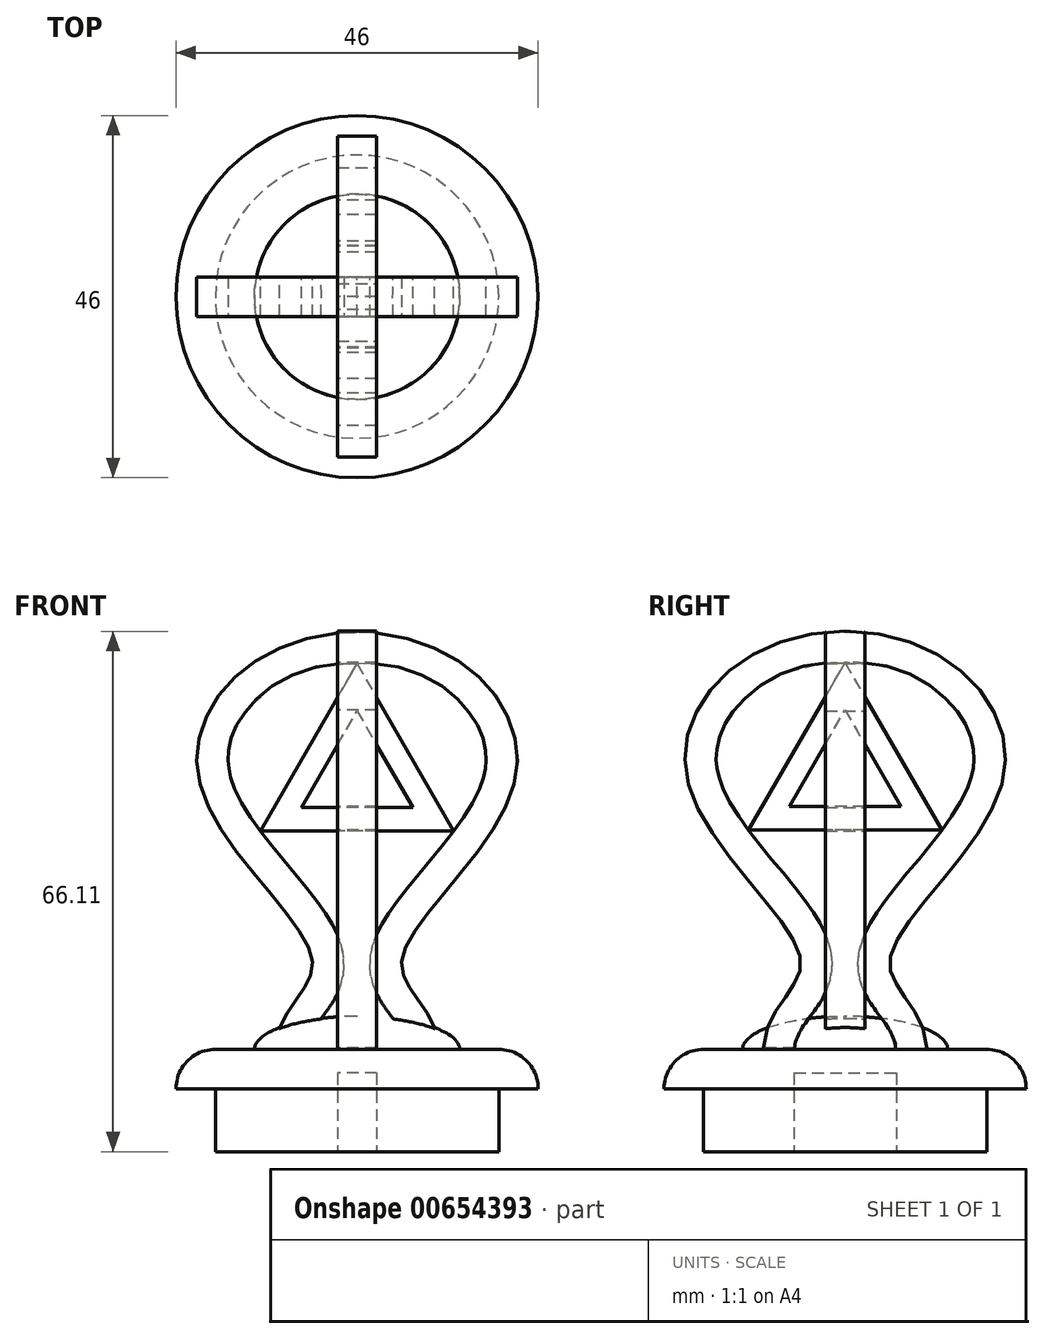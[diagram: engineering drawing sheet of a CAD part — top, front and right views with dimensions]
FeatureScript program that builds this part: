
annotation { "Feature Type Name" : "Feature", "Feature Type Description" : "" }
export const myFeature = defineFeature(function(context is Context, id is Id, definition is map)
    precondition{}
    {
        {
            var Q0;
            Q0=qCreatedBy(makeId("Front.planeOp"),FACE);
            var sketch = newSketch(context, id + "F0", { "sketchPlane" : qUnion([Q0])});
            skLineSegment(sketch, "E0.bottom", {"start": v(0, 0) * mm, "end": v(-18, 0) * mm});
            skLineSegment(sketch, "E0.top", {"start": v(-13.04, 13) * mm, "end": v(-18, 13) * mm});
            skLineSegment(sketch, "E0.left", {"start": v(0, 0) * mm, "end": v(0, 13) * mm});
            skLineSegment(sketch, "E0.right", {"start": v(-18, 0) * mm, "end": v(-18, 8) * mm});
            skLineSegment(sketch, "E1.bottom", {"start": v(-18, 13) * mm, "end": v(-18, 13) * mm});
            skLineSegment(sketch, "E1.top", {"start": v(-18, 8) * mm, "end": v(-23, 8) * mm});
            skLineSegment(sketch, "E1.right", {"start": v(-23, 8) * mm, "end": v(-23, 8) * mm});
            skPoint(sketch, "E2.visualSharp", {"position": v(-23, 13) * mm});
            skArc(sketch, "E2.filletArc", {"start": v(-18, 13) * mm, "mid": v(-21.54, 11.54) * mm, "end": v(-23, 8) * mm});
            skEllipticalArc(sketch, "E3", {});
            skLineSegment(sketch, "E4", {"start": v(0, 17.2) * mm, "end": v(0, 13) * mm});
            const initialGuessF0  = {"E3": [0, 0.013, -1, 0, 0.013036161661148071, 0.004200676908314866, 4.71238898038469, 0]};
            skSetInitialGuess(sketch, initialGuessF0);
            skSolve(sketch);
        }
        {
            var Q0;
            Q0 = qSketchRegion(id + "F0", true);
            var Q1;
            Q1=sQuery(id+"F0.wireOp",EDGE,"E0.left");
            revolve(context, id + "F1", {"entities" : qUnion([Q0]), "axis" : qUnion([Q1]), "revolveType" : RevolveType.FULL});
        }
        {
            var Q0;
            Q0=qCreatedBy(makeId("Front.planeOp"),FACE);
            var sketch = newSketch(context, id + "F2", { "sketchPlane" : qUnion([Q0])});
            skFitSpline(sketch, "E5", {"points": [v(-10.42, 12.76) * mm, v(-5.67, 24.14) * mm, v(-20.19, 47.76) * mm, v(0, 66) * mm], "startDerivative": vector(1.6, 66.34) * mm, "endDerivative": vector(103.18, 0) * mm});
            skFitSpline(sketch, "E6.0", {"points": [v(-6.42, 12.66) * mm, v(-6.41, 13.06) * mm, v(-6.31, 13.74) * mm, v(-5.98, 14.67) * mm, v(-5.43, 15.66) * mm, v(-4.66, 16.77) * mm, v(-3.72, 18.05) * mm, v(-2.87, 19.36) * mm, v(-2.25, 20.66) * mm, v(-1.87, 21.78) * mm, v(-1.68, 22.84) * mm, v(-1.64, 23.73) * mm, v(-1.66, 24.3) * mm, v(-1.7, 24.76) * mm, v(-1.77, 25.2) * mm, v(-1.88, 25.75) * mm, v(-2.05, 26.36) * mm, v(-2.32, 27.15) * mm, v(-2.73, 28.07) * mm, v(-3.3, 29.12) * mm, v(-3.92, 30.13) * mm, v(-4.83, 31.46) * mm, v(-6.07, 33.09) * mm, v(-7.68, 35.06) * mm, v(-9.34, 37.04) * mm, v(-10.98, 39.04) * mm, v(-12.52, 41.05) * mm, v(-13.9, 43.02) * mm, v(-15.01, 44.94) * mm, v(-15.69, 46.44) * mm, v(-16.05, 47.56) * mm, v(-16.21, 48.22) * mm, v(-16.3, 48.73) * mm, v(-16.36, 49.24) * mm, v(-16.39, 49.87) * mm, v(-16.35, 50.63) * mm, v(-16.21, 51.64) * mm, v(-15.86, 52.91) * mm, v(-15.15, 54.44) * mm, v(-14.15, 55.92) * mm, v(-12.43, 57.8) * mm, v(-9.6, 59.86) * mm, v(-5.26, 61.56) * mm, v(-1.83, 62) * mm, v(0, 62) * mm]});
            skFitSpline(sketch, "E7.MirrorCS", {"points": [v(10.42, 12.76) * mm, v(5.67, 24.14) * mm, v(20.19, 47.76) * mm, v(0, 66) * mm], "startDerivative": vector(-1.6, 66.34) * mm, "endDerivative": vector(-103.18, 0) * mm});
            skFitSpline(sketch, "E8.0", {"points": [v(6.42, 12.66) * mm, v(6.41, 13.06) * mm, v(6.31, 13.74) * mm, v(5.98, 14.67) * mm, v(5.43, 15.66) * mm, v(4.66, 16.77) * mm, v(3.72, 18.05) * mm, v(2.87, 19.36) * mm, v(2.25, 20.66) * mm, v(1.87, 21.78) * mm, v(1.68, 22.84) * mm, v(1.64, 23.73) * mm, v(1.66, 24.3) * mm, v(1.7, 24.76) * mm, v(1.77, 25.2) * mm, v(1.88, 25.75) * mm, v(2.05, 26.36) * mm, v(2.32, 27.15) * mm, v(2.73, 28.07) * mm, v(3.3, 29.12) * mm, v(3.92, 30.13) * mm, v(4.83, 31.46) * mm, v(6.07, 33.09) * mm, v(7.68, 35.06) * mm, v(9.34, 37.04) * mm, v(10.98, 39.04) * mm, v(12.52, 41.05) * mm, v(13.9, 43.02) * mm, v(15.01, 44.94) * mm, v(15.69, 46.44) * mm, v(16.05, 47.56) * mm, v(16.21, 48.22) * mm, v(16.3, 48.73) * mm, v(16.36, 49.24) * mm, v(16.39, 49.87) * mm, v(16.35, 50.63) * mm, v(16.21, 51.64) * mm, v(15.86, 52.91) * mm, v(15.15, 54.44) * mm, v(14.15, 55.92) * mm, v(12.43, 57.8) * mm, v(9.6, 59.86) * mm, v(5.26, 61.56) * mm, v(1.83, 62) * mm, v(0, 62) * mm]});
            skLineSegment(sketch, "E9", {"start": v(-12.27, 40.74) * mm, "end": v(0, 62) * mm});
            skLineSegment(sketch, "E10", {"start": v(0, 62) * mm, "end": v(12.27, 40.74) * mm});
            skLineSegment(sketch, "E11", {"start": v(12.27, 40.74) * mm, "end": v(-12.27, 40.74) * mm});
            skLineSegment(sketch, "E12", {"start": v(-6.4, 13.05) * mm, "end": v(-10.42, 13.05) * mm});
            skLineSegment(sketch, "E13", {"start": v(6.4, 13.04) * mm, "end": v(10.42, 13.04) * mm});
            skLineSegment(sketch, "E14.0", {"start": v(-7.08, 43.74) * mm, "end": v(0, 56) * mm});
            skLineSegment(sketch, "E14.1", {"start": v(7.08, 43.74) * mm, "end": v(-7.08, 43.74) * mm});
            skLineSegment(sketch, "E14.2", {"start": v(0, 56) * mm, "end": v(7.08, 43.74) * mm});
            skSolve(sketch);
        }
        {
            var Q0;
            {var subQ0=sQuery(id+"F2.wireOp",EDGE,"E7.MirrorCS");var subQ1=sQuery(id+"F2.wireOp",EDGE,"E5");var subQ2=makeQuery(id+"F2.imprint","INTERSECT",VERTEX,{"derivedFrom":[subQ1,subQ0]});Q0=makeQuery(id+"F2.imprint","IMPRINT",FACE,{"disambiguationData":[TD([[makeQuery(id+"F2.imprint","IMPRINT",EDGE,{"disambiguationData":[TD([[subQ2,1.0]])],"derivedFrom":subQ1}),-1.0]])]});}
            var Q1;
            Q1=makeQuery(id+"F2.imprint","IMPRINT",FACE,{"disambiguationData":[TD([[makeQuery(id+"F2.imprint","IMPRINT",EDGE,{"derivedFrom":sQuery(id+"F2.wireOp",EDGE,"E9")}),-1.0]])]});
            extrude(context, id + "F3", {"entities" : qUnion([Q0, Q1]), "operationType" : NewBodyOperationType.ADD, "depth" : 2.5 * mm, "offsetDistance" : 25 * mm, "hasSecondDirection" : true, "secondDirectionOppositeDirection" : true, "secondDirectionDepth" : 2.5 * mm});
        }
        {
            var Q0;
            Q0=qCreatedBy(makeId("Right.planeOp"),FACE);
            var sketch = newSketch(context, id + "F4", { "sketchPlane" : qUnion([Q0])});
            skFitSpline(sketch, "E15", {"points": [v(-10.42, 12.87) * mm, v(-5.67, 24.26) * mm, v(-20.19, 47.87) * mm, v(0, 66.11) * mm], "startDerivative": vector(1.6, 66.34) * mm, "endDerivative": vector(103.18, 0) * mm});
            skFitSpline(sketch, "E16.0", {"points": [v(-6.42, 12.77) * mm, v(-6.41, 13.17) * mm, v(-6.31, 13.85) * mm, v(-5.98, 14.78) * mm, v(-5.43, 15.78) * mm, v(-4.66, 16.88) * mm, v(-3.72, 18.16) * mm, v(-2.87, 19.47) * mm, v(-2.25, 20.77) * mm, v(-1.87, 21.9) * mm, v(-1.68, 22.95) * mm, v(-1.64, 23.84) * mm, v(-1.66, 24.42) * mm, v(-1.7, 24.87) * mm, v(-1.77, 25.32) * mm, v(-1.88, 25.86) * mm, v(-2.05, 26.47) * mm, v(-2.32, 27.26) * mm, v(-2.73, 28.18) * mm, v(-3.3, 29.23) * mm, v(-3.92, 30.24) * mm, v(-4.83, 31.57) * mm, v(-6.07, 33.2) * mm, v(-7.68, 35.17) * mm, v(-9.34, 37.15) * mm, v(-10.98, 39.15) * mm, v(-12.52, 41.16) * mm, v(-13.9, 43.14) * mm, v(-15.01, 45.05) * mm, v(-15.69, 46.56) * mm, v(-16.05, 47.68) * mm, v(-16.21, 48.34) * mm, v(-16.3, 48.84) * mm, v(-16.36, 49.35) * mm, v(-16.39, 49.98) * mm, v(-16.35, 50.74) * mm, v(-16.21, 51.75) * mm, v(-15.86, 53.03) * mm, v(-15.15, 54.55) * mm, v(-14.15, 56.03) * mm, v(-12.43, 57.9) * mm, v(-9.6, 59.97) * mm, v(-5.26, 61.67) * mm, v(-1.83, 62.11) * mm, v(0, 62.11) * mm]});
            skFitSpline(sketch, "E17.MirrorCS", {"points": [v(10.42, 12.87) * mm, v(5.67, 24.26) * mm, v(20.19, 47.87) * mm, v(0, 66.11) * mm], "startDerivative": vector(-1.6, 66.34) * mm, "endDerivative": vector(-103.18, 0) * mm});
            skFitSpline(sketch, "E18.0", {"points": [v(6.42, 12.77) * mm, v(6.41, 13.17) * mm, v(6.31, 13.85) * mm, v(5.98, 14.78) * mm, v(5.43, 15.78) * mm, v(4.66, 16.88) * mm, v(3.72, 18.16) * mm, v(2.87, 19.47) * mm, v(2.25, 20.77) * mm, v(1.87, 21.9) * mm, v(1.68, 22.95) * mm, v(1.64, 23.84) * mm, v(1.66, 24.42) * mm, v(1.7, 24.87) * mm, v(1.77, 25.32) * mm, v(1.88, 25.86) * mm, v(2.05, 26.47) * mm, v(2.32, 27.26) * mm, v(2.73, 28.18) * mm, v(3.3, 29.23) * mm, v(3.92, 30.24) * mm, v(4.83, 31.57) * mm, v(6.07, 33.2) * mm, v(7.68, 35.17) * mm, v(9.34, 37.15) * mm, v(10.98, 39.15) * mm, v(12.52, 41.16) * mm, v(13.9, 43.14) * mm, v(15.01, 45.05) * mm, v(15.69, 46.56) * mm, v(16.05, 47.68) * mm, v(16.21, 48.34) * mm, v(16.3, 48.84) * mm, v(16.36, 49.35) * mm, v(16.39, 49.98) * mm, v(16.35, 50.74) * mm, v(16.21, 51.75) * mm, v(15.86, 53.03) * mm, v(15.15, 54.55) * mm, v(14.15, 56.03) * mm, v(12.43, 57.9) * mm, v(9.6, 59.97) * mm, v(5.26, 61.67) * mm, v(1.83, 62.11) * mm, v(0, 62.11) * mm]});
            skLineSegment(sketch, "E19", {"start": v(-12.27, 40.85) * mm, "end": v(0, 62.11) * mm});
            skLineSegment(sketch, "E20", {"start": v(0, 62.11) * mm, "end": v(12.27, 40.85) * mm});
            skLineSegment(sketch, "E21", {"start": v(12.27, 40.85) * mm, "end": v(-12.27, 40.85) * mm});
            skLineSegment(sketch, "E22", {"start": v(-6.4, 13.17) * mm, "end": v(-10.42, 13.17) * mm});
            skLineSegment(sketch, "E23", {"start": v(6.4, 13.14) * mm, "end": v(10.42, 13.14) * mm});
            skLineSegment(sketch, "E24.0", {"start": v(-7.08, 43.85) * mm, "end": v(0, 56.11) * mm});
            skLineSegment(sketch, "E24.1", {"start": v(7.08, 43.85) * mm, "end": v(-7.08, 43.85) * mm});
            skLineSegment(sketch, "E24.2", {"start": v(0, 56.11) * mm, "end": v(7.08, 43.85) * mm});
            skSolve(sketch);
        }
        {
            var Q0;
            {var subQ0=sQuery(id+"F4.wireOp",EDGE,"E17.MirrorCS");var subQ1=sQuery(id+"F4.wireOp",EDGE,"E15");var subQ2=makeQuery(id+"F4.imprint","INTERSECT",VERTEX,{"derivedFrom":[subQ1,subQ0]});Q0=makeQuery(id+"F4.imprint","IMPRINT",FACE,{"disambiguationData":[TD([[makeQuery(id+"F4.imprint","IMPRINT",EDGE,{"disambiguationData":[TD([[subQ2,1.0]])],"derivedFrom":subQ1}),-1.0]])]});}
            var Q1;
            Q1=makeQuery(id+"F4.imprint","IMPRINT",FACE,{"disambiguationData":[TD([[makeQuery(id+"F4.imprint","IMPRINT",EDGE,{"derivedFrom":sQuery(id+"F4.wireOp",EDGE,"E19")}),-1.0]])]});
            extrude(context, id + "F5", {"entities" : qUnion([Q0, Q1]), "depth" : 2.5 * mm, "offsetDistance" : 25 * mm, "hasSecondDirection" : true, "secondDirectionOppositeDirection" : true, "secondDirectionDepth" : 2.5 * mm});
        }
        {
            var Q0;
            Q0=makeQuery(id+"F1.opRevolve","SWEPT_FACE",FACE,{"disambiguationData":[OSD([sQuery(id+"F0.wireOp",EDGE,"E0.bottom")])]});
            var sketch = newSketch(context, id + "F6", { "sketchPlane" : qUnion([Q0])});
            skLineSegment(sketch, "E25.bottom", {"start": v(2.5, 6.5) * mm, "end": v(-2.5, 6.5) * mm});
            skLineSegment(sketch, "E25.top", {"start": v(2.5, -6.5) * mm, "end": v(-2.5, -6.5) * mm});
            skLineSegment(sketch, "E25.left", {"start": v(2.5, 6.5) * mm, "end": v(2.5, -6.5) * mm});
            skLineSegment(sketch, "E25.right", {"start": v(-2.5, 6.5) * mm, "end": v(-2.5, -6.5) * mm});
            skPoint(sketch, "E25.middle", {"position": v(0, 0) * mm});
            skSolve(sketch);
        }
        {
            var Q0;
            Q0 = qSketchRegion(id + "F6", true);
            extrude(context, id + "F7", {"entities" : qUnion([Q0]), "operationType" : NewBodyOperationType.REMOVE, "oppositeDirection" : true, "depth" : 10 * mm, "offsetDistance" : 25 * mm});
        }
    });
